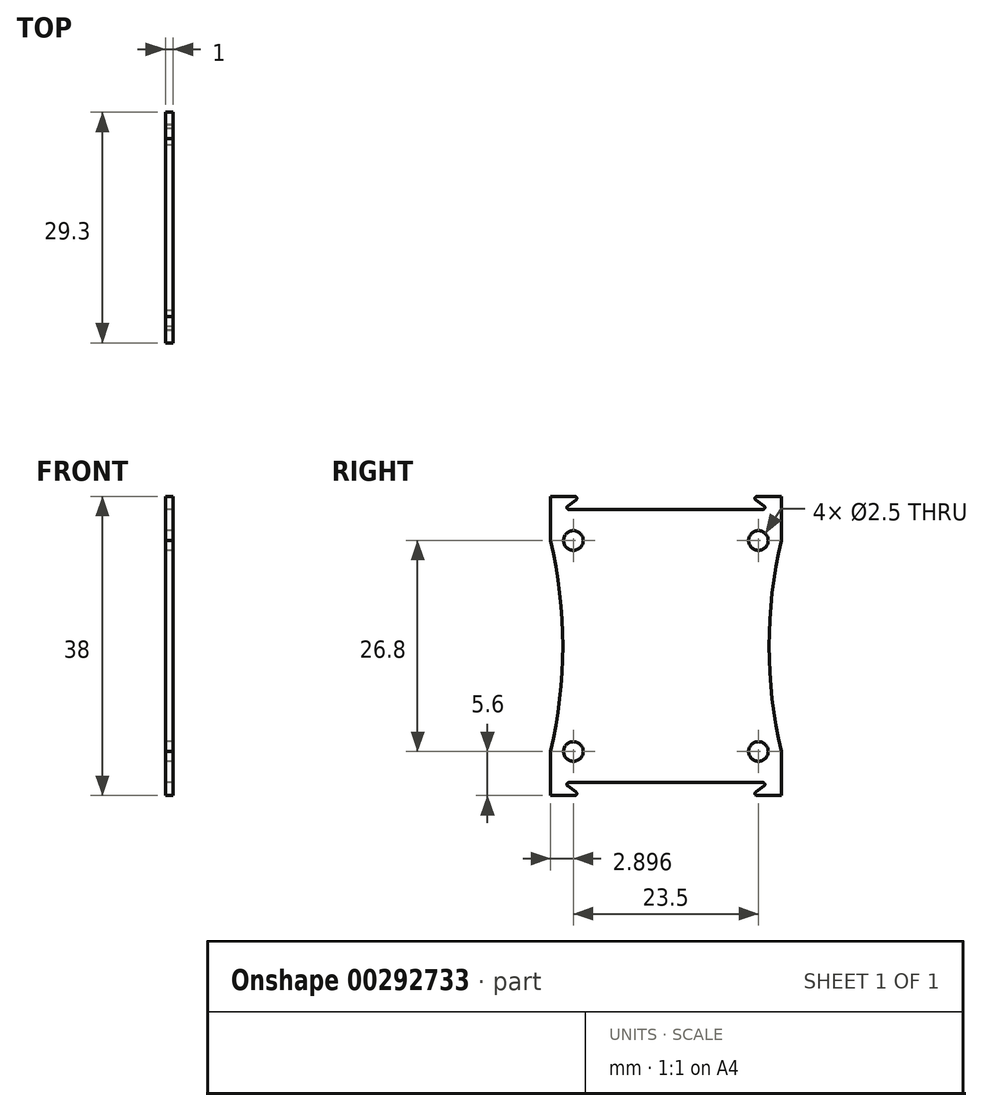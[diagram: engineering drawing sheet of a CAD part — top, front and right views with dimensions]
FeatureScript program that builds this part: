
annotation { "Feature Type Name" : "Feature", "Feature Type Description" : "" }
export const myFeature = defineFeature(function(context is Context, id is Id, definition is map)
    precondition{}
    {
        {
            var Q0;
            Q0=qCreatedBy(makeId("Right.planeOp"),FACE);
            var sketch = newSketch(context, id + "F0", { "sketchPlane" : qUnion([Q0])});
            skPoint(sketch, "E0.middle", {"position": v(-0.04, 0) * mm});
            skLineSegment(sketch, "E1.0", {"start": v(-0.04, 17.35) * mm, "end": v(-12.36, 17.35) * mm});
            skLineSegment(sketch, "E1.3", {"start": v(-13.14, 17.35) * mm, "end": v(-13.14, 0) * mm, "construction": true});
            skLineSegment(sketch, "E2.bottom", {"start": v(-11.61, 19) * mm, "end": v(-14.7, 19) * mm});
            skLineSegment(sketch, "E2.right", {"start": v(-14.7, 19) * mm, "end": v(-14.7, 13.4) * mm});
            skLineSegment(sketch, "E3", {"start": v(-0.04, 0) * mm, "end": v(-0.04, 16) * mm, "construction": true});
            skLineSegment(sketch, "E4", {"start": v(-0.04, 0) * mm, "end": v(-11.8, 0) * mm, "construction": true});
            skArc(sketch, "E5", {"start": v(-10.83, 14.2) * mm, "mid": v(-13.04, 13.4) * mm, "end": v(-10.83, 12.6) * mm, "construction": true});
            skArc(sketch, "E6", {"start": v(-13.14, 0) * mm, "mid": v(-13.53, 6.74) * mm, "end": v(-14.7, 13.4) * mm});
            skLineSegment(sketch, "E7", {"start": v(-11.8, 13.4) * mm, "end": v(-14.7, 13.4) * mm, "construction": true});
            skArc(sketch, "E8.0", {"start": v(-11.8, 11.35) * mm, "mid": v(-10.86, 11.58) * mm, "end": v(-10.13, 12.2) * mm, "construction": true});
            skLineSegment(sketch, "E9.trimOffspring", {"start": v(-11.8, 11.35) * mm, "end": v(-11.8, 0) * mm, "construction": true});
            skLineSegment(sketch, "E10", {"start": v(-11.8, 13.4) * mm, "end": v(-9.74, 13.4) * mm, "construction": true});
            skLineSegment(sketch, "E11.0", {"start": v(-10.83, 12.6) * mm, "end": v(-10.33, 12.6) * mm, "construction": true});
            skLineSegment(sketch, "E12", {"start": v(-11.8, 16) * mm, "end": v(-11.8, 11.35) * mm, "construction": true});
            skLineSegment(sketch, "E13.trimOffspring", {"start": v(-10.83, 14.2) * mm, "end": v(-9.9, 14.2) * mm, "construction": true});
            skLineSegment(sketch, "E14", {"start": v(-10.83, 14.2) * mm, "end": v(-10.83, 12.6) * mm, "construction": true});
            skLineSegment(sketch, "E15", {"start": v(-9.9, 14.2) * mm, "end": v(-9.9, 15.05) * mm, "construction": true});
            skLineSegment(sketch, "E16", {"start": v(-9.9, 15.05) * mm, "end": v(-8.44, 15.05) * mm, "construction": true});
            skLineSegment(sketch, "E17", {"start": v(-8.44, 15.05) * mm, "end": v(-8.44, 16) * mm, "construction": true});
            skLineSegment(sketch, "E18", {"start": v(-8.44, 16) * mm, "end": v(-6.44, 16) * mm, "construction": true});
            skLineSegment(sketch, "E19", {"start": v(-6.44, 16) * mm, "end": v(-6.44, 15.05) * mm, "construction": true});
            skLineSegment(sketch, "E20", {"start": v(-6.44, 15.05) * mm, "end": v(-5.44, 15.05) * mm, "construction": true});
            skLineSegment(sketch, "E21", {"start": v(-5.44, 15.05) * mm, "end": v(-5.44, 16) * mm, "construction": true});
            skLineSegment(sketch, "E22", {"start": v(-5.44, 16) * mm, "end": v(-0.04, 16) * mm, "construction": true});
            skLineSegment(sketch, "E23", {"start": v(-10.83, 14.2) * mm, "end": v(-10.83, 19) * mm, "construction": true});
            skLineSegment(sketch, "E24", {"start": v(-12.5, 17.8) * mm, "end": v(-11.47, 18.55) * mm});
            skPoint(sketch, "E25.visualSharp", {"position": v(-10.83, 19) * mm});
            skArc(sketch, "E25.filletArc", {"start": v(-11.47, 18.55) * mm, "mid": v(-11.38, 18.83) * mm, "end": v(-11.61, 19) * mm});
            skPoint(sketch, "E26.visualSharp", {"position": v(-13.14, 17.35) * mm});
            skArc(sketch, "E26.filletArc", {"start": v(-12.5, 17.8) * mm, "mid": v(-12.6, 17.52) * mm, "end": v(-12.36, 17.35) * mm});
            skPoint(sketch, "E27.visualSharp", {"position": v(-9.9, 12.6) * mm});
            skArc(sketch, "E27.filletArc", {"start": v(-10.13, 12.2) * mm, "mid": v(-10.1, 12.46) * mm, "end": v(-10.33, 12.6) * mm, "construction": true});
            skArc(sketch, "E28.MirrorCS", {"start": v(10.04, 12.2) * mm, "mid": v(10.02, 12.46) * mm, "end": v(10.24, 12.6) * mm, "construction": true});
            skLineSegment(sketch, "E29.MirrorCS", {"start": v(10.75, 12.6) * mm, "end": v(10.24, 12.6) * mm, "construction": true});
            skLineSegment(sketch, "E30.MirrorCS", {"start": v(11.7, 13.4) * mm, "end": v(9.66, 13.4) * mm, "construction": true});
            skLineSegment(sketch, "E31.MirrorCS", {"start": v(10.75, 14.2) * mm, "end": v(10.75, 12.6) * mm, "construction": true});
            skLineSegment(sketch, "E32.MirrorCS", {"start": v(9.82, 15.05) * mm, "end": v(8.36, 15.05) * mm, "construction": true});
            skLineSegment(sketch, "E33.MirrorCS", {"start": v(12.42, 17.8) * mm, "end": v(11.38, 18.55) * mm});
            skLineSegment(sketch, "E34.MirrorCS", {"start": v(10.75, 14.2) * mm, "end": v(9.82, 14.2) * mm, "construction": true});
            skLineSegment(sketch, "E35.MirrorCS", {"start": v(9.82, 14.2) * mm, "end": v(9.82, 15.05) * mm, "construction": true});
            skArc(sketch, "E36.MirrorCS", {"start": v(11.7, 11.35) * mm, "mid": v(10.77, 11.58) * mm, "end": v(10.04, 12.2) * mm, "construction": true});
            skArc(sketch, "E37.MirrorCS", {"start": v(12.42, 17.8) * mm, "mid": v(12.51, 17.52) * mm, "end": v(12.28, 17.35) * mm});
            skArc(sketch, "E38.MirrorCS", {"start": v(11.38, 18.55) * mm, "mid": v(11.29, 18.83) * mm, "end": v(11.53, 19) * mm});
            skLineSegment(sketch, "E39.MirrorCS", {"start": v(5.36, 15.05) * mm, "end": v(5.36, 16) * mm, "construction": true});
            skLineSegment(sketch, "E40.MirrorCS", {"start": v(6.36, 15.05) * mm, "end": v(5.36, 15.05) * mm, "construction": true});
            skLineSegment(sketch, "E41.MirrorCS", {"start": v(8.36, 15.05) * mm, "end": v(8.36, 16) * mm, "construction": true});
            skLineSegment(sketch, "E42.MirrorCS", {"start": v(8.36, 16) * mm, "end": v(6.36, 16) * mm, "construction": true});
            skLineSegment(sketch, "E43.MirrorCS", {"start": v(6.36, 16) * mm, "end": v(6.36, 15.05) * mm, "construction": true});
            skLineSegment(sketch, "E44.MirrorCS", {"start": v(11.7, 13.4) * mm, "end": v(14.6, 13.4) * mm, "construction": true});
            skLineSegment(sketch, "E45.MirrorCS", {"start": v(10.75, 14.2) * mm, "end": v(10.75, 19) * mm, "construction": true});
            skPoint(sketch, "E46.MirrorP", {"position": v(9.82, 12.6) * mm});
            skLineSegment(sketch, "E47.MirrorCS", {"start": v(11.7, 16) * mm, "end": v(11.7, 11.35) * mm, "construction": true});
            skLineSegment(sketch, "E48.MirrorCS", {"start": v(11.53, 19) * mm, "end": v(14.6, 19) * mm});
            skArc(sketch, "E49.MirrorCS", {"start": v(10.75, 14.2) * mm, "mid": v(12.96, 13.4) * mm, "end": v(10.75, 12.6) * mm, "construction": true});
            skLineSegment(sketch, "E50.MirrorCS", {"start": v(11.7, 11.35) * mm, "end": v(11.7, 0) * mm, "construction": true});
            skPoint(sketch, "E51.MirrorP", {"position": v(10.75, 19) * mm});
            skPoint(sketch, "E52.MirrorP", {"position": v(13.06, 17.35) * mm});
            skLineSegment(sketch, "E53.MirrorCS", {"start": v(-0.04, 0) * mm, "end": v(11.7, 0) * mm, "construction": true});
            skArc(sketch, "E54.MirrorCS", {"start": v(13.06, 0) * mm, "mid": v(13.44, 6.74) * mm, "end": v(14.6, 13.4) * mm});
            skLineSegment(sketch, "E55.MirrorCS", {"start": v(5.36, 16) * mm, "end": v(-0.04, 16) * mm, "construction": true});
            skLineSegment(sketch, "E56.MirrorCS", {"start": v(-0.04, 17.35) * mm, "end": v(12.28, 17.35) * mm});
            skLineSegment(sketch, "E57.MirrorCS", {"start": v(13.06, 17.35) * mm, "end": v(13.06, 0) * mm, "construction": true});
            skLineSegment(sketch, "E58.MirrorCS", {"start": v(14.6, 19) * mm, "end": v(14.6, 13.4) * mm});
            skLineSegment(sketch, "E59.MirrorCS", {"start": v(-10.83, -12.6) * mm, "end": v(-10.33, -12.6) * mm, "construction": true});
            skArc(sketch, "E60.MirrorCS", {"start": v(-10.13, -12.2) * mm, "mid": v(-10.1, -12.46) * mm, "end": v(-10.33, -12.6) * mm, "construction": true});
            skLineSegment(sketch, "E61.MirrorCS", {"start": v(-11.8, -13.4) * mm, "end": v(-9.74, -13.4) * mm, "construction": true});
            skLineSegment(sketch, "E62.MirrorCS", {"start": v(11.7, -13.4) * mm, "end": v(9.66, -13.4) * mm, "construction": true});
            skLineSegment(sketch, "E63.MirrorCS", {"start": v(10.75, -12.6) * mm, "end": v(10.24, -12.6) * mm, "construction": true});
            skArc(sketch, "E64.MirrorCS", {"start": v(10.04, -12.2) * mm, "mid": v(10.02, -12.46) * mm, "end": v(10.24, -12.6) * mm, "construction": true});
            skLineSegment(sketch, "E65.MirrorCS", {"start": v(-10.83, -14.2) * mm, "end": v(-10.83, -12.6) * mm, "construction": true});
            skLineSegment(sketch, "E66.MirrorCS", {"start": v(-12.5, -17.8) * mm, "end": v(-11.47, -18.55) * mm});
            skLineSegment(sketch, "E67.MirrorCS", {"start": v(12.42, -17.8) * mm, "end": v(11.38, -18.55) * mm});
            skLineSegment(sketch, "E68.MirrorCS", {"start": v(-10.83, -14.2) * mm, "end": v(-9.9, -14.2) * mm, "construction": true});
            skArc(sketch, "E69.MirrorCS", {"start": v(12.42, -17.8) * mm, "mid": v(12.51, -17.52) * mm, "end": v(12.28, -17.35) * mm});
            skArc(sketch, "E70.MirrorCS", {"start": v(-12.5, -17.8) * mm, "mid": v(-12.6, -17.52) * mm, "end": v(-12.36, -17.35) * mm});
            skLineSegment(sketch, "E71.MirrorCS", {"start": v(10.75, -14.2) * mm, "end": v(10.75, -12.6) * mm, "construction": true});
            skArc(sketch, "E72.MirrorCS", {"start": v(11.38, -18.55) * mm, "mid": v(11.29, -18.83) * mm, "end": v(11.53, -19) * mm});
            skArc(sketch, "E73.MirrorCS", {"start": v(-11.47, -18.55) * mm, "mid": v(-11.38, -18.83) * mm, "end": v(-11.61, -19) * mm});
            skLineSegment(sketch, "E74.MirrorCS", {"start": v(9.82, -14.2) * mm, "end": v(9.82, -15.05) * mm, "construction": true});
            skArc(sketch, "E75.MirrorCS", {"start": v(-11.8, -11.35) * mm, "mid": v(-10.86, -11.58) * mm, "end": v(-10.13, -12.2) * mm, "construction": true});
            skLineSegment(sketch, "E76.MirrorCS", {"start": v(10.75, -14.2) * mm, "end": v(9.82, -14.2) * mm, "construction": true});
            skLineSegment(sketch, "E77.MirrorCS", {"start": v(-9.9, -14.2) * mm, "end": v(-9.9, -15.05) * mm, "construction": true});
            skLineSegment(sketch, "E78.MirrorCS", {"start": v(-8.44, -15.05) * mm, "end": v(-8.44, -16) * mm, "construction": true});
            skLineSegment(sketch, "E79.MirrorCS", {"start": v(-5.44, -15.05) * mm, "end": v(-5.44, -16) * mm, "construction": true});
            skLineSegment(sketch, "E80.MirrorCS", {"start": v(-6.44, -16) * mm, "end": v(-6.44, -15.05) * mm, "construction": true});
            skLineSegment(sketch, "E81.MirrorCS", {"start": v(-6.44, -15.05) * mm, "end": v(-5.44, -15.05) * mm, "construction": true});
            skLineSegment(sketch, "E82.MirrorCS", {"start": v(-9.9, -15.05) * mm, "end": v(-8.44, -15.05) * mm, "construction": true});
            skArc(sketch, "E83.MirrorCS", {"start": v(11.7, -11.35) * mm, "mid": v(10.77, -11.58) * mm, "end": v(10.04, -12.2) * mm, "construction": true});
            skLineSegment(sketch, "E84.MirrorCS", {"start": v(5.36, -15.05) * mm, "end": v(5.36, -16) * mm, "construction": true});
            skLineSegment(sketch, "E85.MirrorCS", {"start": v(-8.44, -16) * mm, "end": v(-6.44, -16) * mm, "construction": true});
            skLineSegment(sketch, "E86.MirrorCS", {"start": v(8.36, -15.05) * mm, "end": v(8.36, -16) * mm, "construction": true});
            skLineSegment(sketch, "E87.MirrorCS", {"start": v(6.36, -15.05) * mm, "end": v(5.36, -15.05) * mm, "construction": true});
            skLineSegment(sketch, "E88.MirrorCS", {"start": v(6.36, -16) * mm, "end": v(6.36, -15.05) * mm, "construction": true});
            skLineSegment(sketch, "E89.MirrorCS", {"start": v(8.36, -16) * mm, "end": v(6.36, -16) * mm, "construction": true});
            skLineSegment(sketch, "E90.MirrorCS", {"start": v(9.82, -15.05) * mm, "end": v(8.36, -15.05) * mm, "construction": true});
            skLineSegment(sketch, "E91.MirrorCS", {"start": v(11.7, -16) * mm, "end": v(11.7, -11.35) * mm, "construction": true});
            skPoint(sketch, "E92.MirrorP", {"position": v(-9.9, -12.6) * mm});
            skLineSegment(sketch, "E93.MirrorCS", {"start": v(-10.83, -14.2) * mm, "end": v(-10.83, -19) * mm, "construction": true});
            skLineSegment(sketch, "E94.MirrorCS", {"start": v(-11.8, -16) * mm, "end": v(-11.8, -11.35) * mm, "construction": true});
            skLineSegment(sketch, "E95.MirrorCS", {"start": v(-11.61, -19) * mm, "end": v(-14.7, -19) * mm});
            skLineSegment(sketch, "E96.MirrorCS", {"start": v(-11.8, -13.4) * mm, "end": v(-14.7, -13.4) * mm, "construction": true});
            skPoint(sketch, "E97.MirrorP", {"position": v(-10.83, -19) * mm});
            skLineSegment(sketch, "E98.MirrorCS", {"start": v(14.6, -19) * mm, "end": v(14.6, -13.4) * mm});
            skLineSegment(sketch, "E99.MirrorCS", {"start": v(-13.14, -17.35) * mm, "end": v(-13.14, 0) * mm, "construction": true});
            skPoint(sketch, "E100.MirrorP", {"position": v(-13.14, -17.35) * mm});
            skLineSegment(sketch, "E101.MirrorCS", {"start": v(-11.8, -11.35) * mm, "end": v(-11.8, 0) * mm, "construction": true});
            skPoint(sketch, "E102.MirrorP", {"position": v(10.75, -19) * mm});
            skLineSegment(sketch, "E103.MirrorCS", {"start": v(5.36, -16) * mm, "end": v(-0.04, -16) * mm, "construction": true});
            skLineSegment(sketch, "E104.MirrorCS", {"start": v(11.7, -11.35) * mm, "end": v(11.7, 0) * mm, "construction": true});
            skLineSegment(sketch, "E105.MirrorCS", {"start": v(10.75, -14.2) * mm, "end": v(10.75, -19) * mm, "construction": true});
            skPoint(sketch, "E106.MirrorP", {"position": v(9.82, -12.6) * mm});
            skLineSegment(sketch, "E107.MirrorCS", {"start": v(-0.04, -17.35) * mm, "end": v(12.28, -17.35) * mm});
            skLineSegment(sketch, "E108.MirrorCS", {"start": v(-5.44, -16) * mm, "end": v(-0.04, -16) * mm, "construction": true});
            skLineSegment(sketch, "E109.MirrorCS", {"start": v(13.06, -17.35) * mm, "end": v(13.06, 0) * mm, "construction": true});
            skArc(sketch, "E110.MirrorCS", {"start": v(10.75, -14.2) * mm, "mid": v(12.96, -13.4) * mm, "end": v(10.75, -12.6) * mm, "construction": true});
            skPoint(sketch, "E111.MirrorP", {"position": v(13.06, -17.35) * mm});
            skArc(sketch, "E112.MirrorCS", {"start": v(-10.83, -14.2) * mm, "mid": v(-13.04, -13.4) * mm, "end": v(-10.83, -12.6) * mm, "construction": true});
            skLineSegment(sketch, "E113.MirrorCS", {"start": v(11.53, -19) * mm, "end": v(14.6, -19) * mm});
            skLineSegment(sketch, "E114.MirrorCS", {"start": v(-0.04, 0) * mm, "end": v(-0.04, -16) * mm, "construction": true});
            skLineSegment(sketch, "E115.MirrorCS", {"start": v(-14.7, -19) * mm, "end": v(-14.7, -13.4) * mm});
            skLineSegment(sketch, "E116.MirrorCS", {"start": v(-0.04, -17.35) * mm, "end": v(-12.36, -17.35) * mm});
            skLineSegment(sketch, "E117.MirrorCS", {"start": v(11.7, -13.4) * mm, "end": v(14.6, -13.4) * mm, "construction": true});
            skArc(sketch, "E118.MirrorCS", {"start": v(-13.14, 0) * mm, "mid": v(-13.53, -6.74) * mm, "end": v(-14.7, -13.4) * mm});
            skArc(sketch, "E119.MirrorCS", {"start": v(13.06, 0) * mm, "mid": v(13.44, -6.74) * mm, "end": v(14.6, -13.4) * mm});
            skSolve(sketch);
        }
        {
            var Q0;
            Q0=makeQuery(id+"F0.imprint","IMPRINT",FACE,{"disambiguationData":[TD([[makeQuery(id+"F0.imprint","IMPRINT",EDGE,{"derivedFrom":sQuery(id+"F0.wireOp",EDGE,"E1.0")}),1.0]])]});
            extrude(context, id + "F1", {"entities" : qUnion([Q0]), "depth" : 1 * mm});
        }
        {
            var Q0;
            Q0=makeQuery(id+"F0.imprint","IMPRINT",FACE,{"disambiguationData":[TD([[makeQuery(id+"F0.imprint","IMPRINT",EDGE,{"derivedFrom":sQuery(id+"F0.wireOp",EDGE,"E1.0")}),1.0]])]});
            var sketch = newSketch(context, id + "F2", { "sketchPlane" : qUnion([Q0])});
            skCircle(sketch, "E120", {"center": v(11.7, 13.4) * mm, "radius": 1.25 * mm});
            skCircle(sketch, "E121", {"center": v(-11.8, 13.4) * mm, "radius": 1.25 * mm});
            skCircle(sketch, "E122", {"center": v(-11.8, -13.4) * mm, "radius": 1.25 * mm});
            skCircle(sketch, "E123", {"center": v(11.7, -13.4) * mm, "radius": 1.25 * mm});
            skSolve(sketch);
        }
        {
            var Q0;
            Q0 = qSketchRegion(id + "F2", true);
            extrude(context, id + "F3", {"entities" : qUnion([Q0]), "operationType" : NewBodyOperationType.REMOVE, "endBound" : BoundingType.UP_TO_NEXT, "depth" : 25.4 * mm});
        }
    });
